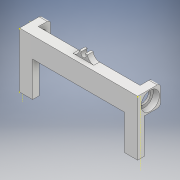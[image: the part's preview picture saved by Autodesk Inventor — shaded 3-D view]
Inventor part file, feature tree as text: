
AUTODESK INVENTOR PART (.ipt)
format: ipt  version: 2018 (Build 220112000, 112)  size: 945,152 bytes
history: native  units: mm
features: sketch x41, extrude x34, fillet x4
ambient origin geometry x8: Origin, YZ Plane, XZ Plane, XY Plane, X Axis, Y Axis, Z Axis, Center Point
bodies: Solid1 (feature_tree)
feature tree (79):
  extrude  "Extrusion1"  Depth=80.0mm
  extrude  "Extrusion2"  Depth=12.0mm
  sketch  "Sketch3"  dims[d5=12.0mm d6=14.5mm]
  extrude  "Extrusion3"  Depth=14.5mm
  extrude  "Extrusion4"  Depth=2.0mm
  extrude  "Extrusion5"  Depth=6.0mm TaperAngle=0.0deg
  sketch  "Sketch7"  dims[d15=10.0mm d16=25.0mm]
  extrude  "Extrusion6"  Depth=25.0mm
  extrude  "Extrusion7"  Depth=25.0mm
  extrude  "Extrusion8"  Depth=10.0mm
  fillet  "Fillet1"  Radius=10.0mm
  fillet  "Fillet2"  Radius=10.0mm
  extrude  "Extrusion9"  Depth=7.5mm TaperAngle=0.0deg
  extrude  "Extrusion10"  Depth=4.0mm
  fillet  "Fillet3"  Radius=3.0mm
  extrude  "Extrusion11"  Depth=21.0mm
  extrude  "Extrusion12"  Depth=41.0mm
  extrude  "Extrusion13"  Depth=42.0mm
  extrude  "Extrusion14"  Depth=38.0mm
  extrude  "Extrusion15"  Depth=45.0mm TaperAngle=0.0deg
  extrude  "Extrusion16"  Depth=3.0mm TaperAngle=0.0deg
  extrude  "Extrusion17"  Depth=3.0mm
  extrude  "Extrusion18"  Depth=39.5mm
  extrude  "Extrusion19"  Depth=7.25mm
  extrude  "Extrusion20"  Depth=125.0mm
  extrude  "Extrusion21"  Depth=10.0mm
  sketch  "Sketch24"  dims[d65=66.0mm d66=3.5mm d67=0.0mm]
  extrude  "Extrusion22"  Depth=10.0mm TaperAngle=0.0deg
  extrude  "Extrusion23"  Depth=12.0mm
  extrude  "Extrusion24"  Depth=3.5mm TaperAngle=0.0deg
  extrude  "Extrusion25"  Depth=2.0mm
  extrude  "Extrusion26"  Depth=2.0mm TaperAngle=0.0deg
  sketch  "Sketch30"  dims[d81=4.0mm d82=4.0mm]
  extrude  "Extrusion27"  Depth=16.0mm
  extrude  "Extrusion28"  Depth=2.0mm
  extrude  "Extrusion29"  Depth=2.0mm TaperAngle=0.0deg
  sketch  "Sketch34"  dims[d91=5.0mm d92=16.0mm d93=5.0mm]
  extrude  "Extrusion30"  Depth=4.0mm
  extrude  "Extrusion31"  Depth=2.0mm TaperAngle=0.0deg
  extrude  "Extrusion32"  Depth=150.0mm TaperAngle=0.0deg
  sketch  "Sketch38"  dims[d98=43.0mm d99=0.0mm]
  extrude  "Extrusion33"  Depth=16.0mm
  sketch  "Sketch40"  dims[d101=38.75mm]
  extrude  "Extrusion34"  Depth=16.0mm
  fillet  "Fillet4"  Radius=5.0mm
  sketch  "Sketch1"  dims[d0=145.0mm d1=80.0mm]
  sketch  "Sketch2"  dims[d2=3.0mm d3=0.0mm d4=12.0mm]
  sketch  "Sketch4"  dims[d7=2.0mm d8=2.0mm]
  sketch  "Sketch5"  dims[d9=6.0mm d10=0.0mm d11=0.5mm d12=0.0mm]
  sketch  "Sketch6"  dims[d13=10.0mm d14=25.0mm]
  sketch  "Sketch8"  dims[d17=25.0mm d18=0.0mm d19=22.5mm d20=10.0mm d21=0.0mm d22=10.0mm]
  sketch  "Sketch9"  dims[d23=2.5mm d24=0.0mm d25=7.5mm d26=0.0mm]
  sketch  "Sketch10"  dims[d27=10.0mm d28=0.0mm d29=4.0mm d30=3.0mm]
  sketch  "Sketch11"  dims[d31=1.0mm d32=21.0mm]
  sketch  "Sketch12"  dims[d33=38.0mm d34=41.0mm]
  sketch  "Sketch13"  dims[d35=38.0mm d36=42.0mm]
  sketch  "Sketch14"  dims[d37=41.0mm d38=38.0mm]
  sketch  "Sketch15"  dims[d39=42.0mm d40=45.0mm d41=0.0mm]
  sketch  "Sketch16"  dims[d42=12.5mm d43=3.0mm d44=0.0mm]
  sketch  "Sketch17"  dims[d45=3.0mm d46=39.5mm]
  sketch  "Sketch18"  dims[d47=39.5mm d48=39.5mm]
  sketch  "Sketch19"  dims[d49=45.0mm d50=0.0mm d51=7.25mm]
  sketch  "Sketch20"  dims[d52=4.0mm d53=7.75mm d54=0.0mm d55=0.0mm d56=125.0mm]
  sketch  "Sketch21"  dims[d57=10.0mm d58=0.0mm d59=1.0mm]
  sketch  "Sketch22"  dims[d60=14.5mm d61=10.0mm d62=0.0mm]
  sketch  "Sketch23"  dims[d63=16.0mm d64=12.0mm]
  sketch  "Sketch25"  dims[d68=4.0mm d69=2.0mm]
  sketch  "Sketch26"  dims[d70=4.0mm d71=2.0mm d72=0.0mm]
  sketch  "Sketch27"  dims[d73=2.0mm d74=0.0mm d75=16.0mm]
  sketch  "Sketch28"  dims[d76=2.0mm d77=2.0mm]
  sketch  "Sketch29"  dims[d78=2.0mm d79=3.5mm d80=0.0mm]
  sketch  "Sketch31"  dims[d83=4.0mm d84=2.0mm d85=0.0mm]
  sketch  "Sketch32"  dims[d86=15.5mm d87=150.0mm d88=0.0mm]
  sketch  "Sketch33"  dims[d89=12.0mm d90=16.0mm]
  sketch  "Sketch35"  dims[d94=12.0mm]
  sketch  "Sketch36"  dims[d95=3.0mm]
  sketch  "Sketch37"  dims[d96=43.0mm d97=0.0mm]
  sketch  "Sketch39"  dims[d100=38.75mm]
  sketch  "Sketch41"  dims[d102=5.0mm d103=0.0mm d104=500.0mm d105=0.0mm d106=45.0mm d107=0.0mm d108=45.0mm d109=0.0mm d110=38.75mm d111=38.75mm d112=45.0mm d113=0.0mm d114=3.5mm d115=0.0mm d116=43.0mm d117=0.0mm d118=100.0mm d119=0.0mm d120=200.0mm d121=0.0mm d122=1.5mm d123=0.0mm d124=5.0mm d125=10.0mm d126=10.0mm d127=6.35mm d128=7.0mm d129=0.0mm d130=2.75mm d131=7.0mm d132=0.0mm d133=7.75mm]
